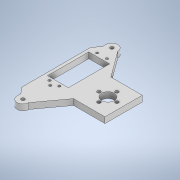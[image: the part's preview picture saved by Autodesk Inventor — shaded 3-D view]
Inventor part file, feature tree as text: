
AUTODESK INVENTOR PART (.ipt)
format: ipt  version: 2022 (Build 260153000, 153)  size: 146,944 bytes
history: native  units: mm
features: extrude x1, sketch x1
ambient origin geometry x8: Origin, YZ Plane, XZ Plane, XY Plane, X Axis, Y Axis, Z Axis, Center Point
bodies: Solid1 (feature_tree)
feature tree (2):
  extrude  "Extrusion1"  Depth=19.0mm
  sketch  "Sketch1"  dims[d0=19.0mm d1=19.0mm d2=90.0deg d3=32.0mm d4=68.5mm d5=35.0mm d8=13.0mm d10=3.5mm d18=10.75mm d22=2.5mm d28=40.0mm d30=360.0deg d35=12.0mm d39=6.0mm d40=0.0mm]
